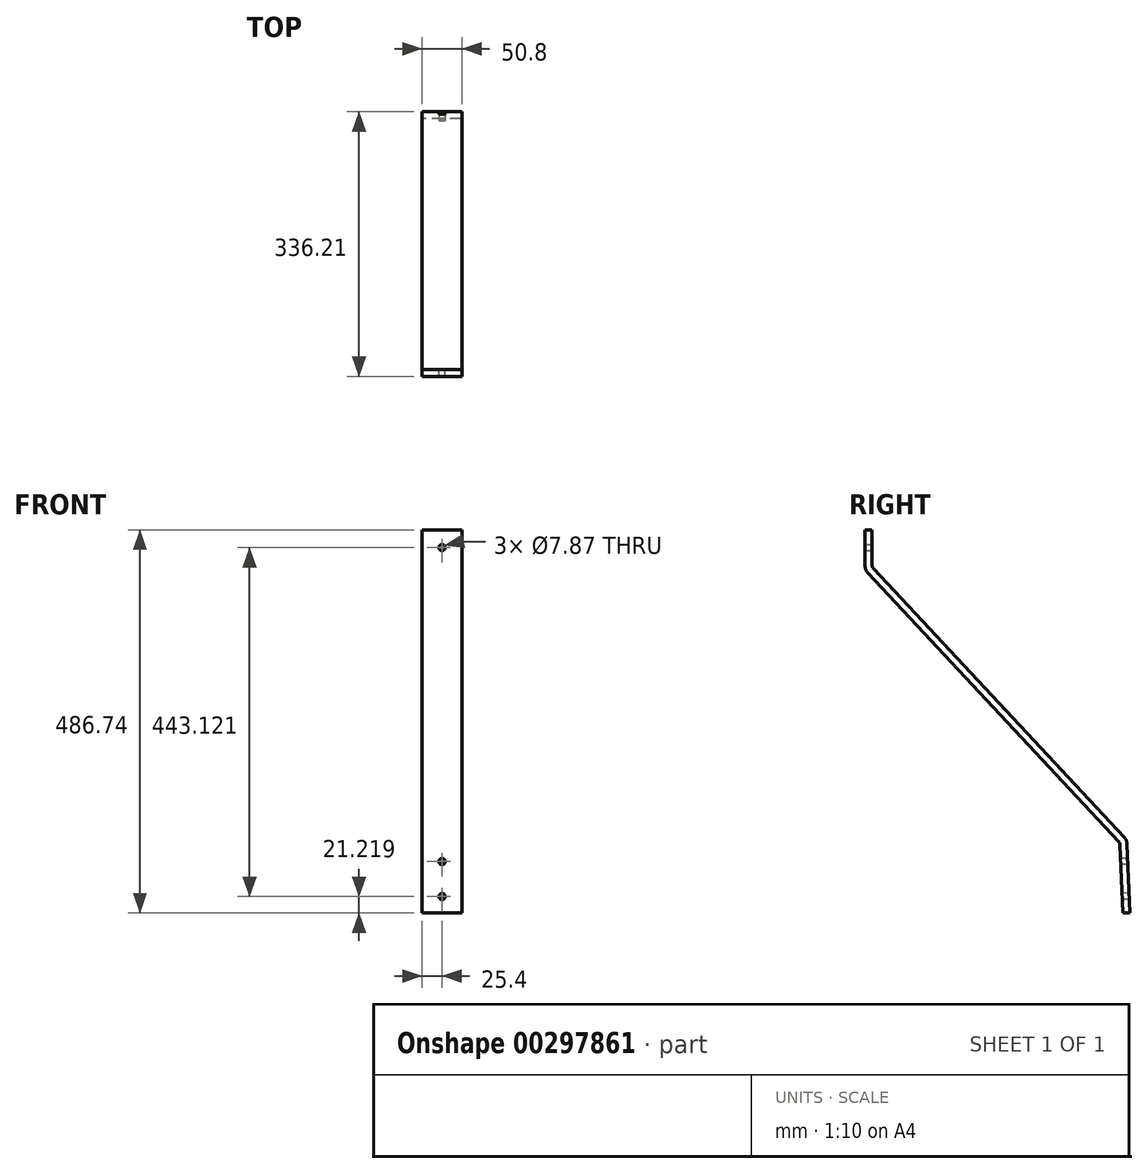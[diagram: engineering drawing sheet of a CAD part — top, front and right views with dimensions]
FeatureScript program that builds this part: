
annotation { "Feature Type Name" : "Feature", "Feature Type Description" : "" }
export const myFeature = defineFeature(function(context is Context, id is Id, definition is map)
    precondition{}
    {
        {
            var Q0;
            Q0=qCreatedBy(makeId("Right.planeOp"),FACE);
            var sketch = newSketch(context, id + "F0", { "sketchPlane" : qUnion([Q0])});
            skLineSegment(sketch, "E0", {"start": v(0, 155.27) * mm, "end": v(0, -236.22) * mm, "construction": true});
            skLineSegment(sketch, "E1.0", {"start": v(323.85, 180.67) * mm, "end": v(323.85, -191.77) * mm, "construction": true});
            skLineSegment(sketch, "E2", {"start": v(0, 180.67) * mm, "end": v(323.85, 180.67) * mm, "construction": true});
            skLineSegment(sketch, "E3.0", {"start": v(0, 206.07) * mm, "end": v(374.65, 206.07) * mm, "construction": true});
            skLineSegment(sketch, "E4", {"start": v(0, -236.22) * mm, "end": v(323.85, -236.22) * mm, "construction": true});
            skLineSegment(sketch, "E5.0", {"start": v(1.53, -280.67) * mm, "end": v(327.32, -280.67) * mm, "construction": true});
            skLineSegment(sketch, "E6.0", {"start": v(0, 155.27) * mm, "end": v(374.65, 155.27) * mm, "construction": true});
            skLineSegment(sketch, "E7.0", {"start": v(1.53, -191.77) * mm, "end": v(323.85, -191.77) * mm, "construction": true});
            skLineSegment(sketch, "E8", {"start": v(3.41, 151.6) * mm, "end": v(322.24, -190.04) * mm});
            skLineSegment(sketch, "E9", {"start": v(0, 160.27) * mm, "end": v(0, 206.07) * mm});
            skLineSegment(sketch, "E10", {"start": v(323.94, -194.13) * mm, "end": v(327.32, -280.67) * mm});
            skLineSegment(sketch, "E11.0", {"start": v(8.9, 161.27) * mm, "end": v(8.9, 206.07) * mm});
            skLineSegment(sketch, "E11.1", {"start": v(10.6, 156.94) * mm, "end": v(329.38, -184.67) * mm});
            skLineSegment(sketch, "E11.2", {"start": v(332.79, -192.84) * mm, "end": v(336.21, -280.67) * mm});
            skLineSegment(sketch, "E12", {"start": v(0, 206.07) * mm, "end": v(8.9, 206.07) * mm});
            skLineSegment(sketch, "E13", {"start": v(336.21, -280.67) * mm, "end": v(327.32, -280.67) * mm});
            skPoint(sketch, "E14.visualSharp", {"position": v(8.9, 158.77) * mm});
            skArc(sketch, "E14.filletArc", {"start": v(8.9, 161.27) * mm, "mid": v(9.33, 158.94) * mm, "end": v(10.6, 156.94) * mm});
            skPoint(sketch, "E15.visualSharp", {"position": v(323.85, -191.77) * mm});
            skArc(sketch, "E15.filletArc", {"start": v(323.94, -194.13) * mm, "mid": v(323.46, -191.93) * mm, "end": v(322.24, -190.04) * mm});
            skPoint(sketch, "E16.visualSharp", {"position": v(332.6, -188.12) * mm});
            skArc(sketch, "E16.filletArc", {"start": v(332.79, -192.84) * mm, "mid": v(331.82, -188.45) * mm, "end": v(329.38, -184.67) * mm});
            skPoint(sketch, "E17.visualSharp", {"position": v(0, 155.27) * mm});
            skArc(sketch, "E17.filletArc", {"start": v(0, 160.27) * mm, "mid": v(0.88, 155.62) * mm, "end": v(3.41, 151.6) * mm});
            skSolve(sketch);
        }
        {
            var Q0;
            Q0=makeQuery(id+"F0.imprint","IMPRINT",FACE,{"disambiguationData":[TD([[makeQuery(id+"F0.imprint","IMPRINT",EDGE,{"derivedFrom":sQuery(id+"F0.wireOp",EDGE,"E8")}),1.0]])]});
            extrude(context, id + "F1", {"entities" : qUnion([Q0]), "endBound" : BoundingType.SYMMETRIC, "depth" : 50.8 * mm});
        }
        {
            var Q0;
            Q0=makeQuery(id+"F1.opExtrude","SWEPT_FACE",FACE,{"disambiguationData":[OSD([sQuery(id+"F0.wireOp",EDGE,"E11.0")])]});
            var sketch = newSketch(context, id + "F2", { "sketchPlane" : qUnion([Q0])});
            skLineSegment(sketch, "E18", {"start": v(-25.4, 183.67) * mm, "end": v(0, 183.67) * mm, "construction": true});
            skPoint(sketch, "E18.endSnap0", {"position": v(0, 206.07) * mm});
            skPoint(sketch, "E19", {"position": v(0, 183.67) * mm});
            skSolve(sketch);
        }
        {
            var Q0;
            Q0=sQuery(id+"F2.wireOp",VERTEX,"E19");
            var Q1;
            Q1=makeQuery(id+"F1.opExtrude","SWEPT_BODY",BODY,{"disambiguationData":[OSD([sQuery(id+"F0.wireOp",EDGE,"E8"),sQuery(id+"F0.wireOp",EDGE,"E9"),sQuery(id+"F0.wireOp",EDGE,"E10"),sQuery(id+"F0.wireOp",EDGE,"E11.0"),sQuery(id+"F0.wireOp",EDGE,"E11.1"),sQuery(id+"F0.wireOp",EDGE,"E11.2"),sQuery(id+"F0.wireOp",EDGE,"E12"),sQuery(id+"F0.wireOp",EDGE,"E13"),sQuery(id+"F0.wireOp",EDGE,"E14.filletArc"),sQuery(id+"F0.wireOp",EDGE,"E15.filletArc"),sQuery(id+"F0.wireOp",EDGE,"E16.filletArc"),sQuery(id+"F0.wireOp",EDGE,"E17.filletArc")])]});
            hole(context, id + "F3", {"style" : HoleStyle.SIMPLE, "endStyle" : HoleEndStyle.THROUGH, "holeDiameter" : 7.87 * mm, "tappedDepth" : 42.34 * mm, "tapClearance" : 3, "startFromSketch" : true, "locations" : qUnion([Q0]), "scope" : qUnion([Q1])});
        }
        {
            var Q0;
            Q0=makeQuery(id+"F1.opExtrude","SWEPT_FACE",FACE,{"disambiguationData":[OSD([sQuery(id+"F0.wireOp",EDGE,"E10")])]});
            var sketch = newSketch(context, id + "F4", { "sketchPlane" : qUnion([Q0])});
            skLineSegment(sketch, "E20.0", {"start": v(25.4, -206.6) * mm, "end": v(-25.4, -206.6) * mm, "construction": true});
            skLineSegment(sketch, "E21.0", {"start": v(-25.4, -206.6) * mm, "end": v(-25.4, -293.21) * mm, "construction": true});
            skLineSegment(sketch, "E22", {"start": v(-25.4, -249.9) * mm, "end": v(25.4, -249.9) * mm, "construction": true});
            skLineSegment(sketch, "E23", {"start": v(0, -206.6) * mm, "end": v(0, -293.21) * mm, "construction": true});
            skLineSegment(sketch, "E24.0", {"start": v(-25.4, -272.13) * mm, "end": v(25.4, -272.13) * mm, "construction": true});
            skPoint(sketch, "E25", {"position": v(0, -272.13) * mm});
            skPoint(sketch, "E26.MirrorP", {"position": v(0, -227.68) * mm});
            skSolve(sketch);
        }
        {
            var Q0;
            Q0=sQuery(id+"F4.wireOp",VERTEX,"E26.MirrorP");
            var Q1;
            Q1=sQuery(id+"F4.wireOp",VERTEX,"E25");
            var Q2;
            Q2=makeQuery(id+"F1.opExtrude","SWEPT_BODY",BODY,{"disambiguationData":[OSD([sQuery(id+"F0.wireOp",EDGE,"E8"),sQuery(id+"F0.wireOp",EDGE,"E9"),sQuery(id+"F0.wireOp",EDGE,"E10"),sQuery(id+"F0.wireOp",EDGE,"E11.0"),sQuery(id+"F0.wireOp",EDGE,"E11.1"),sQuery(id+"F0.wireOp",EDGE,"E11.2"),sQuery(id+"F0.wireOp",EDGE,"E12"),sQuery(id+"F0.wireOp",EDGE,"E13"),sQuery(id+"F0.wireOp",EDGE,"E14.filletArc"),sQuery(id+"F0.wireOp",EDGE,"E15.filletArc"),sQuery(id+"F0.wireOp",EDGE,"E16.filletArc"),sQuery(id+"F0.wireOp",EDGE,"E17.filletArc")])]});
            hole(context, id + "F5", {"style" : HoleStyle.SIMPLE, "endStyle" : HoleEndStyle.THROUGH, "holeDiameter" : 7.87 * mm, "tappedDepth" : 42.34 * mm, "tapClearance" : 3, "startFromSketch" : true, "locations" : qUnion([Q0, Q1]), "scope" : qUnion([Q2])});
        }
    });
